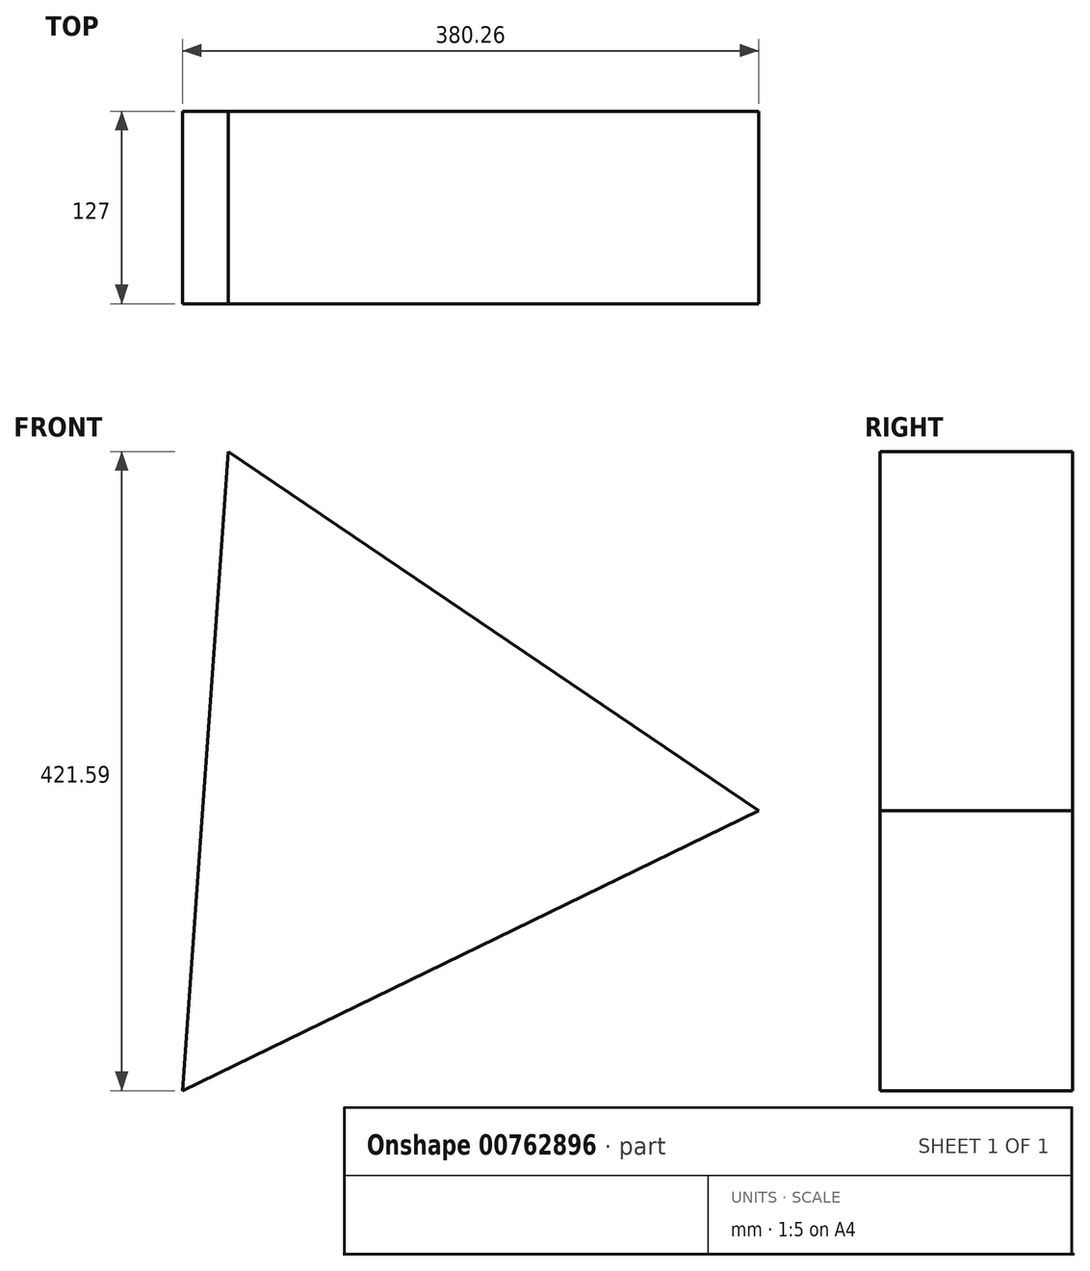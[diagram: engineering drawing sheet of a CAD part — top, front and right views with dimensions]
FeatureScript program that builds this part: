
annotation { "Feature Type Name" : "Feature", "Feature Type Description" : "" }
export const myFeature = defineFeature(function(context is Context, id is Id, definition is map)
    precondition{}
    {
        {
            var Q0;
            Q0=qCreatedBy(makeId("Front.planeOp"),FACE);
            var sketch = newSketch(context, id + "F0", { "sketchPlane" : qUnion([Q0])});
            skCircle(sketch, "E0.cCircle", {"center": v(0, 0) * mm, "radius": 49.45 * mm, "construction": true});
            skLineSegment(sketch, "E0.0", {"start": v(-38.87, 38.74) * mm, "end": v(6.05, 54.55) * mm});
            skLineSegment(sketch, "E0.1", {"start": v(6.05, 54.55) * mm, "end": v(46.42, 29.28) * mm});
            skLineSegment(sketch, "E0.2", {"start": v(46.42, 29.28) * mm, "end": v(51.83, -18.04) * mm});
            skLineSegment(sketch, "E0.3", {"start": v(51.83, -18.04) * mm, "end": v(18.21, -51.77) * mm});
            skLineSegment(sketch, "E0.4", {"start": v(18.21, -51.77) * mm, "end": v(-29.12, -46.52) * mm});
            skLineSegment(sketch, "E0.5", {"start": v(-29.12, -46.52) * mm, "end": v(-54.53, -6.24) * mm});
            skLineSegment(sketch, "E0.6", {"start": v(-54.53, -6.24) * mm, "end": v(-38.87, 38.74) * mm});
            skPoint(sketch, "E0.0.midPoint", {"position": v(-16.4, 46.64) * mm});
            skCircle(sketch, "E1.cCircle", {"center": v(0, 0) * mm, "radius": 80.53 * mm, "construction": true});
            skLineSegment(sketch, "E1.0", {"start": v(-55.34, 70.2) * mm, "end": v(20.37, 87.03) * mm});
            skLineSegment(sketch, "E1.1", {"start": v(20.37, 87.03) * mm, "end": v(80.75, 38.34) * mm});
            skLineSegment(sketch, "E1.2", {"start": v(80.75, 38.34) * mm, "end": v(80.32, -39.23) * mm});
            skLineSegment(sketch, "E1.3", {"start": v(80.32, -39.23) * mm, "end": v(19.4, -87.25) * mm});
            skLineSegment(sketch, "E1.4", {"start": v(19.4, -87.25) * mm, "end": v(-56.12, -69.58) * mm});
            skLineSegment(sketch, "E1.5", {"start": v(-56.12, -69.58) * mm, "end": v(-89.39, 0.5) * mm});
            skLineSegment(sketch, "E1.6", {"start": v(-89.39, 0.5) * mm, "end": v(-55.34, 70.2) * mm});
            skPoint(sketch, "E1.0.midPoint", {"position": v(-17.49, 78.61) * mm});
            skSolve(sketch);
        }
        {
            var Q0;
            Q0=makeQuery(id+"F0.imprint","IMPRINT",FACE,{"disambiguationData":[TD([[makeQuery(id+"F0.imprint","IMPRINT",EDGE,{"derivedFrom":sQuery(id+"F0.wireOp",EDGE,"E0.0")}),-1.0]])]});
            var Q1;
            Q1=makeQuery(id+"F0.imprint","IMPRINT",FACE,{"disambiguationData":[TD([[makeQuery(id+"F0.imprint","IMPRINT",EDGE,{"derivedFrom":sQuery(id+"F0.wireOp",EDGE,"E0.0")}),1.0]])]});
            extrude(context, id + "F1", {"entities" : qUnion([Q0, Q1]), "endBound" : BoundingType.SYMMETRIC, "depth" : 25.4 * mm, "offsetDistance" : 25.4 * mm});
        }
        {
            var Q0;
            Q0=makeQuery(id+"F1.opExtrude","CAP_FACE",FACE,{"disambiguationData":[OSD([sQuery(id+"F0.wireOp",EDGE,"E1.0"),sQuery(id+"F0.wireOp",EDGE,"E1.1"),sQuery(id+"F0.wireOp",EDGE,"E1.2"),sQuery(id+"F0.wireOp",EDGE,"E1.3"),sQuery(id+"F0.wireOp",EDGE,"E1.4"),sQuery(id+"F0.wireOp",EDGE,"E1.5"),sQuery(id+"F0.wireOp",EDGE,"E1.6")])],"isStart":true});
            var sketch = newSketch(context, id + "F2", { "sketchPlane" : qUnion([Q0])});
            skCircle(sketch, "E2.cCircle", {"center": v(0, -4.55) * mm, "radius": 244.03 * mm, "construction": true});
            skLineSegment(sketch, "E2.0", {"start": v(136.85, -206.6) * mm, "end": v(-243.4, -22.04) * mm});
            skLineSegment(sketch, "E2.1", {"start": v(-243.4, -22.04) * mm, "end": v(106.55, 214.99) * mm});
            skLineSegment(sketch, "E2.2", {"start": v(106.55, 214.99) * mm, "end": v(136.85, -206.6) * mm});
            skSolve(sketch);
        }
        {
            var Q0;
            Q0 = qSketchRegion(id + "F2", true);
            extrude(context, id + "F3", {"entities" : qUnion([Q0]), "operationType" : NewBodyOperationType.ADD, "oppositeDirection" : true, "depth" : 127 * mm, "offsetDistance" : 25.4 * mm});
        }
    });
